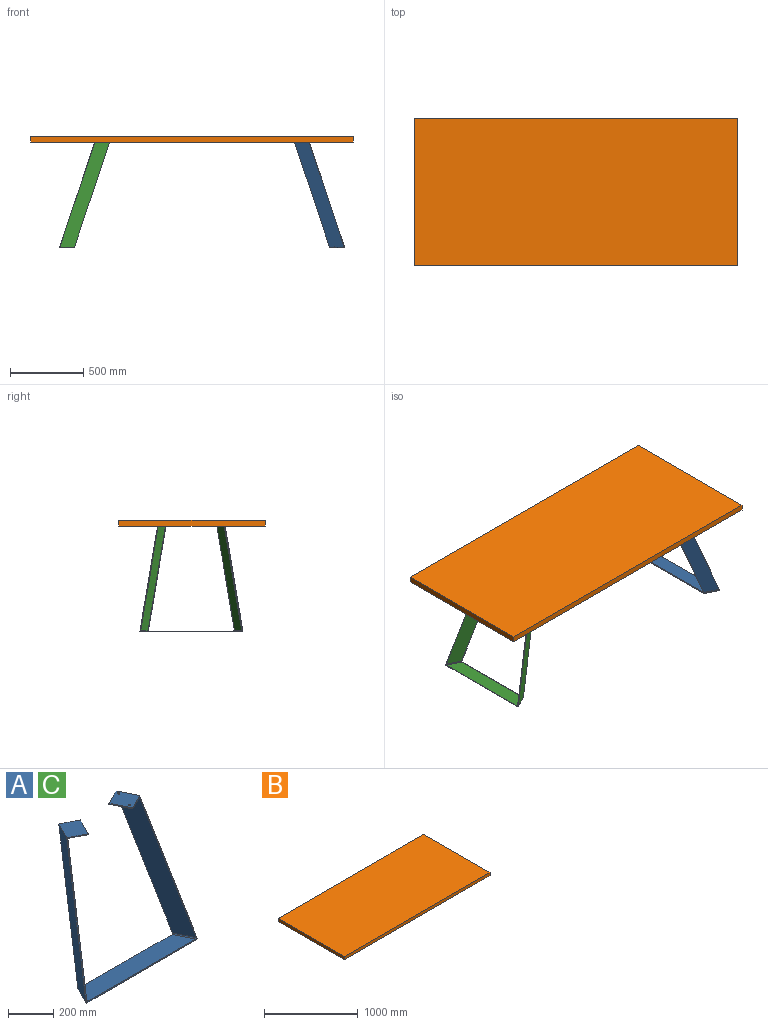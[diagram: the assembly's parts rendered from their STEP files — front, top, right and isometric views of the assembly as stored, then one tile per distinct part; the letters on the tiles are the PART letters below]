
ASSEMBLY  parts=3 mates=2
PART A: 32 faces, bbox 698.9x343.5x720 mm
  f0: plane 690x6.68mm, normal (0,-1,0), area 3456.7mm2, adj f2,f3,f5,f8,f10,f13,f18,f19
  f1: plane 590x6.68mm, normal (0,1,0), area 2956.7mm2, adj f2,f3,f6,f7,f11,f12,f18,f19
  f2: plane 678.82x100mm, normal (0,0,1), area 62882mm2, adj f0,f1,f18,f19
  f3: plane 690x100mm, normal (0,0,-1), area 64000mm2, adj f0,f1,f16,f17
  f4: plane 705x337.9mm, normal (0.89,-0.45,0), area 78821.4mm2, adj f5,f6,f19,f29
  f5: plane 710x241.82mm, normal (-0.42,-0.84,0.35), area 3796.8mm2, adj f0,f4,f8,f9,f19,f27
  f6: plane 710x241.82mm, normal (0.42,0.84,-0.35), area 3796.8mm2, adj f1,f4,f7,f9,f19,f25
  f7: plane 5x4.47mm, normal (0.45,0.89,0), area 19.6mm2, adj f1,f6,f17
  f8: plane 5x4.47mm, normal (-0.45,-0.89,0), area 19.6mm2, adj f0,f5,f17
  f9: plane 715x339.58mm, normal (-0.89,0.45,0), area 79939.4mm2, adj f5,f6,f17,f25,f27,f28
  f10: plane 710x241.82mm, normal (0.42,-0.84,0.35), area 3796.8mm2, adj f0,f13,f14,f15,f18,f23
  f11: plane 710x241.82mm, normal (-0.42,0.84,-0.35), area 3796.8mm2, adj f1,f12,f14,f15,f18,f21
  f12: plane 5x4.47mm, normal (-0.45,0.89,0), area 19.6mm2, adj f1,f11,f16
  f13: plane 5x4.47mm, normal (0.45,-0.89,0), area 19.6mm2, adj f0,f10,f16
  f14: plane 715x339.58mm, normal (0.89,0.45,0), area 79939.4mm2, adj f10,f11,f16,f21,f23,f24
  f15: plane 705x337.9mm, normal (-0.89,-0.45,0), area 78821.4mm2, adj f10,f11,f18,f20
  f16: cylinder r=5mm len=102.24mm, axis (0.45,-0.89,0), area 878.1mm2, adj f3,f12,f13,f14
  f17: cylinder r=5mm len=102.24mm, axis (-0.45,-0.89,0), area 878.1mm2, adj f3,f7,f8,f9
  f18: cylinder r=5mm len=103.91mm, axis (-0.45,0.89,0), area 878.1mm2, adj f0,f1,f2,f10,f11,f15
  f19: cylinder r=5mm len=103.91mm, axis (0.45,0.89,0), area 878.1mm2, adj f0,f1,f2,f4,f5,f6
  f20: plane 142.49x134.97mm, normal (0,0,-1), area 10464.2mm2, adj f15,f21,f22,f23,f30,f31
  f21: plane 89.44x44.72mm, normal (-0.45,0.89,0), area 500mm2, adj f11,f14,f20,f22,f24
  f22: plane 100x50mm, normal (-0.89,-0.45,0), area 559mm2, adj f20,f21,f23,f24
  f23: plane 89.44x44.72mm, normal (0.45,-0.89,0), area 500mm2, adj f10,f14,f20,f22,f24
  f24: plane 144.72x139.44mm, normal (0,0,1), area 11023.3mm2, adj f14,f21,f22,f23,f30,f31
  f25: plane 89.44x44.72mm, normal (0.45,0.89,0), area 500mm2, adj f6,f9,f26,f28,f29
  f26: plane 100x50mm, normal (0.89,-0.45,0), area 559mm2, adj f25,f27,f28,f29
  f27: plane 89.44x44.72mm, normal (-0.45,-0.89,0), area 500mm2, adj f5,f9,f26,f28,f29
  f28: plane 144.72x139.44mm, normal (0,0,1), area 11180.3mm2, adj f9,f25,f26,f27
  f29: plane 142.49x134.97mm, normal (0,0,-1), area 10621.3mm2, adj f4,f25,f26,f27
  f30: cylinder r=5mm len=10mm, axis (0,0,1), area 157.1mm2, adj f20,f24
  f31: cylinder r=5mm len=10mm, axis (0,0,1), area 157.1mm2, adj f20,f24
PART B: 6 faces, bbox 2200x1000x40 mm
  f0: plane 2200x40mm, normal (0,-1,0), area 88000mm2, adj f1,f3,f4,f5
  f1: plane 1000x40mm, normal (1,0,0), area 40000mm2, adj f0,f2,f4,f5
  f2: plane 2200x40mm, normal (0,1,0), area 88000mm2, adj f1,f3,f4,f5
  f3: plane 1000x40mm, normal (-1,0,0), area 40000mm2, adj f0,f2,f4,f5
  f4: plane 2200x1000mm, normal (0,0,1), area 2200000mm2, adj f0,f1,f2,f3
  f5: plane 2200x1000mm, normal (0,0,-1), area 2200000mm2, adj f0,f1,f2,f3
PART C: same geometry as A
PLACE A rot(axis=(0,0,1),90deg) t=(1206.45,473.98,-471.13)mm
PLACE B rot(axis=(0,0,-1),0deg) t=(216.05,471.3,266.37)mm
PLACE C rot(axis=(0,0,-1),90deg) t=(-637.24,476.67,-471.13)mm
MATE planar B.f5 <-> C.f24  axis (0,0,-1) through (216.05,471.3,246.37)mm
MATE planar B.f5 <-> A.f28  axis (0,0,-1) through (216.05,471.3,246.37)mm
